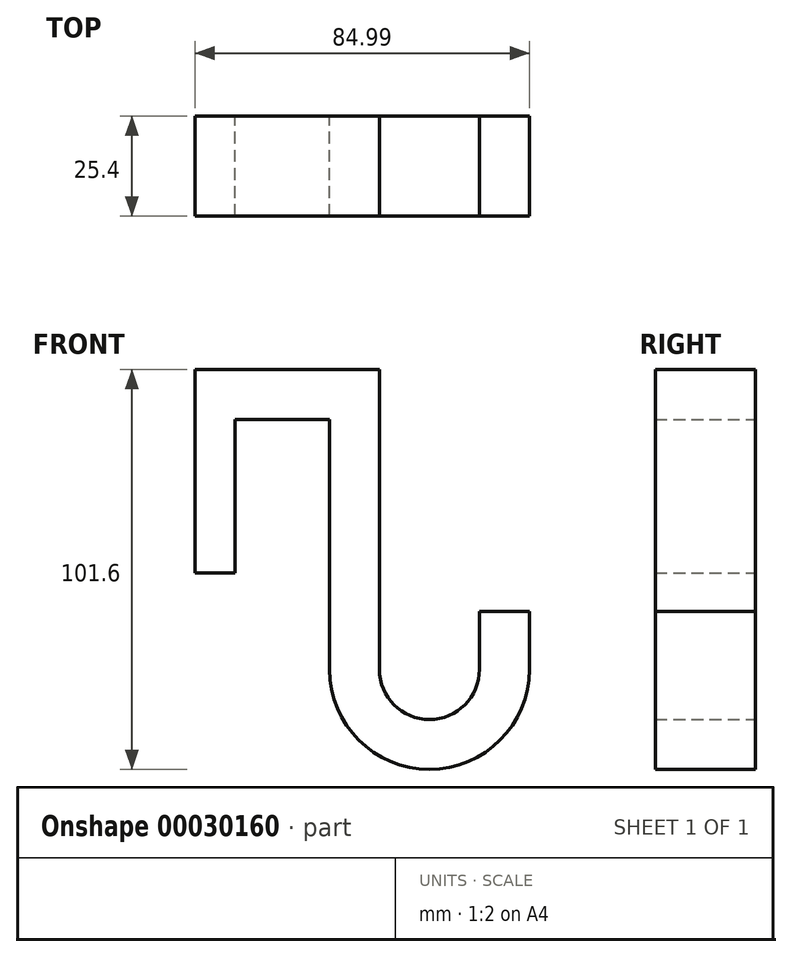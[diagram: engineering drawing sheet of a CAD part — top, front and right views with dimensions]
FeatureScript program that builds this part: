
annotation { "Feature Type Name" : "Feature", "Feature Type Description" : "" }
export const myFeature = defineFeature(function(context is Context, id is Id, definition is map)
    precondition{}
    {
        {
            var Q0;
            Q0=qCreatedBy(makeId("Front.planeOp"),FACE);
            var sketch = newSketch(context, id + "F0", { "sketchPlane" : qUnion([Q0])});
            skLineSegment(sketch, "E0", {"start": v(0, 59.06) * mm, "end": v(0, 7.4) * mm});
            skLineSegment(sketch, "E1", {"start": v(0, 7.4) * mm, "end": v(10.16, 7.4) * mm});
            skLineSegment(sketch, "E2", {"start": v(10.16, 7.4) * mm, "end": v(10.16, 46.36) * mm});
            skLineSegment(sketch, "E3", {"start": v(10.16, 46.36) * mm, "end": v(34.2, 46.36) * mm});
            skLineSegment(sketch, "E4", {"start": v(34.2, 46.36) * mm, "end": v(34.2, -17.14) * mm});
            skArc(sketch, "E5", {"start": v(34.2, -17.14) * mm, "mid": v(59.6, -42.54) * mm, "end": v(85, -17.14) * mm});
            skLineSegment(sketch, "E6", {"start": v(85, -17.14) * mm, "end": v(85, -2.44) * mm});
            skLineSegment(sketch, "E7", {"start": v(85, -2.44) * mm, "end": v(72.3, -2.44) * mm});
            skLineSegment(sketch, "E8", {"start": v(72.3, -2.44) * mm, "end": v(72.3, -17.14) * mm});
            skArc(sketch, "E9", {"start": v(72.3, -17.14) * mm, "mid": v(59.6, -29.84) * mm, "end": v(46.9, -17.14) * mm});
            skLineSegment(sketch, "E10", {"start": v(46.9, -17.14) * mm, "end": v(46.9, 59.06) * mm});
            skLineSegment(sketch, "E11", {"start": v(46.9, 59.06) * mm, "end": v(0, 59.06) * mm});
            skSolve(sketch);
        }
        {
            var Q0;
            Q0 = qSketchRegion(id + "F0", true);
            extrude(context, id + "F1", {"entities" : qUnion([Q0]), "endBound" : BoundingType.SYMMETRIC, "depth" : 25.4 * mm});
        }
    });
